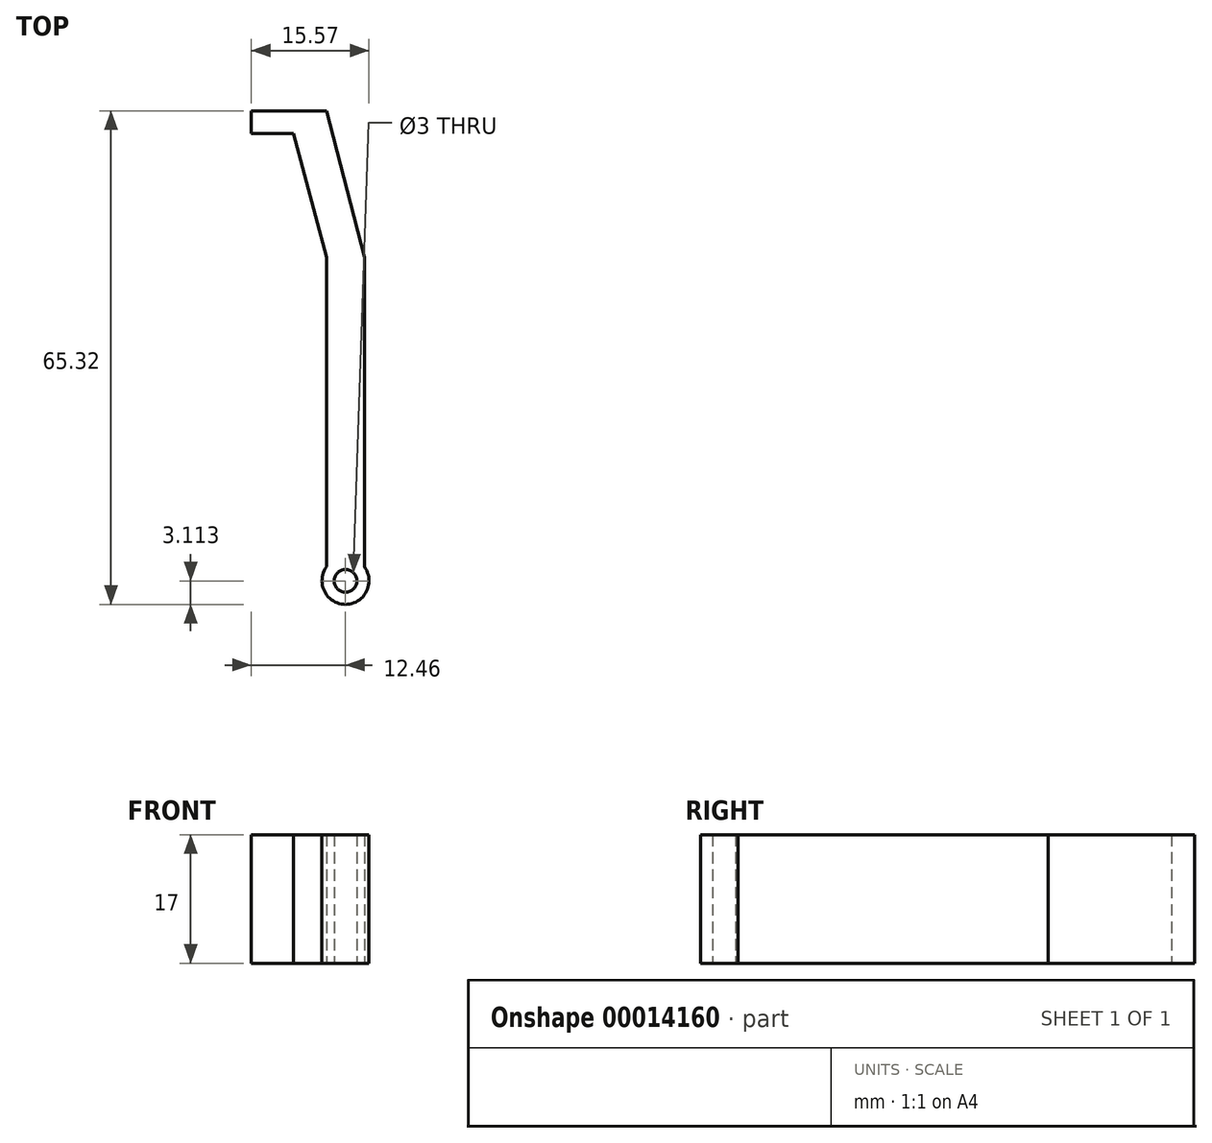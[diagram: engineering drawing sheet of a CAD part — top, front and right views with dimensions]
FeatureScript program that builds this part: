
annotation { "Feature Type Name" : "Feature", "Feature Type Description" : "" }
export const myFeature = defineFeature(function(context is Context, id is Id, definition is map)
    precondition{}
    {
        {
            var Q0;
            Q0=qCreatedBy(makeId("Top.planeOp"),FACE);
            var sketch = newSketch(context, id + "F0", { "sketchPlane" : qUnion([Q0])});
            skLineSegment(sketch, "E0.bottom", {"start": v(0, 0) * mm, "end": v(5, 0) * mm});
            skLineSegment(sketch, "E0.top", {"start": v(0, -41) * mm, "end": v(5, -41) * mm});
            skLineSegment(sketch, "E0.left", {"start": v(0, 0) * mm, "end": v(0, -41) * mm});
            skLineSegment(sketch, "E0.right", {"start": v(5, 0) * mm, "end": v(5, -41) * mm});
            skLineSegment(sketch, "E1", {"start": v(5, 0) * mm, "end": v(0, 19.36) * mm});
            skLineSegment(sketch, "E2", {"start": v(0, 19.36) * mm, "end": v(-4.84, 18.11) * mm});
            skLineSegment(sketch, "E3", {"start": v(-4.84, 18.11) * mm, "end": v(0, 0) * mm});
            skLineSegment(sketch, "E4", {"start": v(0, 19.36) * mm, "end": v(-9.96, 19.36) * mm});
            skLineSegment(sketch, "E5", {"start": v(-9.96, 19.36) * mm, "end": v(-9.96, 16.36) * mm});
            skLineSegment(sketch, "E6", {"start": v(-9.96, 16.36) * mm, "end": v(0.77, 16.36) * mm});
            skLineSegment(sketch, "E7", {"start": v(0.77, 16.36) * mm, "end": v(0, 19.36) * mm});
            skArc(sketch, "E8", {"start": v(0, -41) * mm, "mid": v(2.5, -45.96) * mm, "end": v(5, -41) * mm});
            skCircle(sketch, "E9", {"center": v(2.5, -42.85) * mm, "radius": 1.5 * mm});
            skSolve(sketch);
        }
        {
            var Q0;
            Q0=makeQuery(id+"F0.imprint","IMPRINT",FACE,{"disambiguationData":[TD([[makeQuery(id+"F0.imprint","IMPRINT",EDGE,{"derivedFrom":sQuery(id+"F0.wireOp",EDGE,"E0.bottom")}),-1.0]])]});
            var Q1;
            Q1=makeQuery(id+"F0.imprint","IMPRINT",FACE,{"disambiguationData":[TD([[makeQuery(id+"F0.imprint","IMPRINT",EDGE,{"derivedFrom":sQuery(id+"F0.wireOp",EDGE,"E0.top")}),-1.0]])]});
            var Q2;
            {var subQ4=sQuery(id+"F0.wireOp",EDGE,"E0.bottom");Q2=makeQuery(id+"F0.imprint","IMPRINT",FACE,{"disambiguationData":[TD([[makeQuery(id+"F0.imprint","IMPRINT",EDGE,{"derivedFrom":subQ4}),1.0]])]});}
            var Q3;
            {var subQ4=sQuery(id+"F0.wireOp",EDGE,"E2");Q3=makeQuery(id+"F0.imprint","IMPRINT",FACE,{"disambiguationData":[TD([[makeQuery(id+"F0.imprint","IMPRINT",EDGE,{"derivedFrom":subQ4}),1.0]])]});}
            var Q4;
            {var subQ4=sQuery(id+"F0.wireOp",EDGE,"E2");Q4=makeQuery(id+"F0.imprint","IMPRINT",FACE,{"disambiguationData":[TD([[makeQuery(id+"F0.imprint","IMPRINT",EDGE,{"derivedFrom":subQ4}),-1.0]])]});}
            extrude(context, id + "F1", {"entities" : qUnion([Q0, Q1, Q2, Q3, Q4]), "depth" : 17 * mm});
        }
    });
